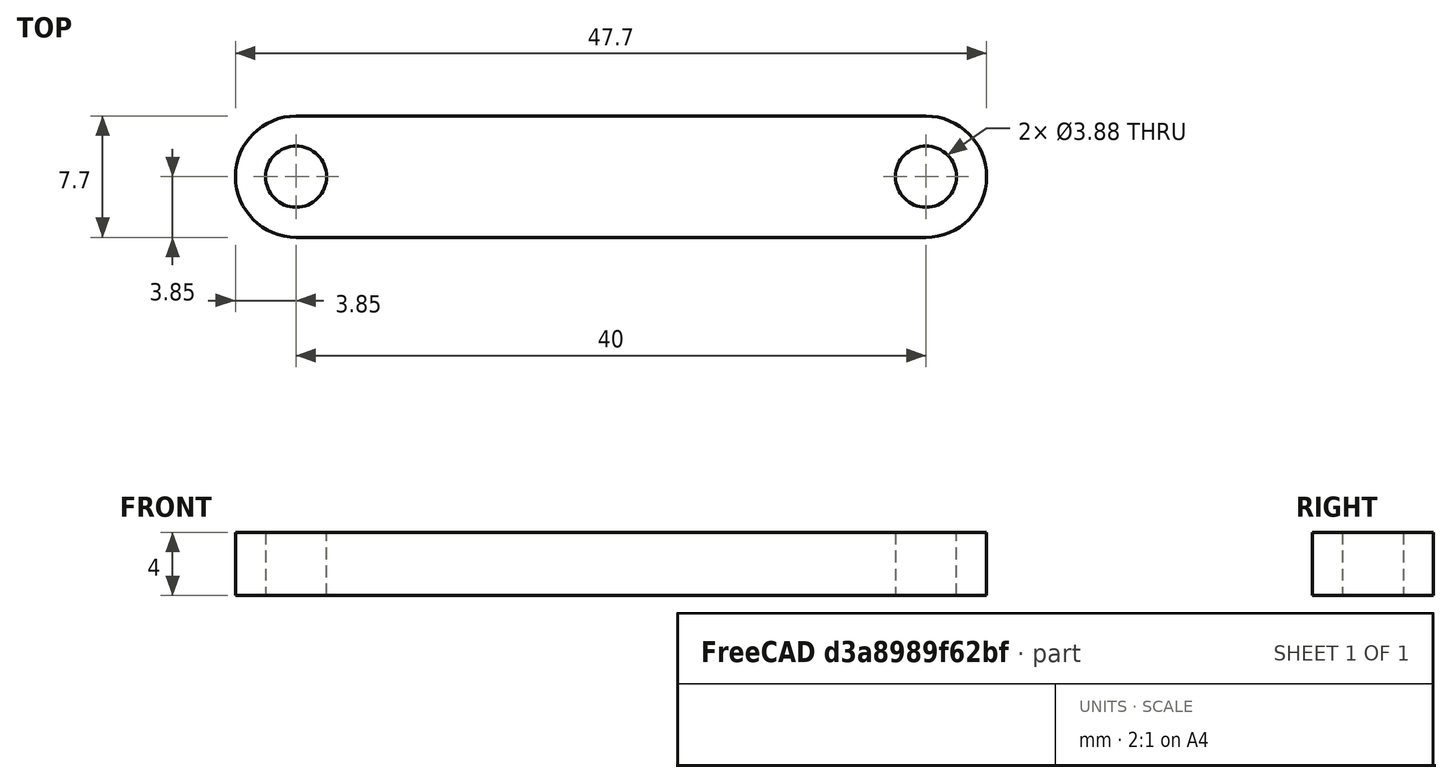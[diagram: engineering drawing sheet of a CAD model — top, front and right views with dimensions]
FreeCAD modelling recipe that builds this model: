
FCSTD DOCUMENT  (FreeCAD 0.20R29410 (Git))
Label: Eslabon1
License: All rights reserved
LicenseURL: http://en.wikipedia.org/wiki/All_rights_reserved
objects: Sketcher::SketchObject×1, Part::Extrusion×1
note: 2 computed .brp shape members not serialized (recipe doc carries the construction recipe); baked Part::Feature solids carry a one-line shape summary decoded from their .brp

FEATURE [Sketcher::SketchObject] Sketch  label="Eslabon 40x7.7mm, hoyo r1.94mm"
  FullyConstrained = true
  sketch-geometry (6):
    g0: LineSegment StartX=2e-16 StartY=3.85 StartZ=0 EndX=40 EndY=3.85 EndZ=0
    g1: LineSegment StartX=-7e-16 StartY=-3.85 StartZ=0 EndX=40 EndY=-3.85 EndZ=0
    g2: ArcOfCircle CenterX=0 CenterY=0 CenterZ=0 NormalX=0 NormalY=0 NormalZ=1 AngleXU=0 Radius=3.85 StartAngle=1.5708 EndAngle=4.71239
    g3: ArcOfCircle CenterX=40 CenterY=1e-16 CenterZ=0 NormalX=0 NormalY=0 NormalZ=1 AngleXU=0 Radius=3.85 StartAngle=4.71239 EndAngle=7.85398
    g4: Circle CenterX=0 CenterY=0 CenterZ=0 NormalX=0 NormalY=0 NormalZ=1 AngleXU=0 Radius=1.94
    g5: Circle CenterX=40 CenterY=1e-16 CenterZ=0 NormalX=0 NormalY=0 NormalZ=1 AngleXU=0 Radius=1.94
  constraints (17):
    c: PointOnObject(g0,g-2)
    c: PointOnObject(g1,g-2)
    c: Horizontal(g0)
    c: Horizontal(g1)
    c: Equal(g0,g1)
    c: Distance(g0) = 40
    c: DistanceY(g1,g0) = 7.7
    c: Coincident(g2,g-1)
    c: Coincident(g2,g0)
    c: Coincident(g3,g0)
    c: Coincident(g3,g1)
    c: Coincident(g4,g2)
    c: Coincident(g5,g3)
    c: Equal(g4,g5)
    c: Radius(g4) = 1.94
    c: Coincident(g1,g2)
    c: Radius(g3) = 3.85
FEATURE [Part::Extrusion] Extrude  label="Extrusion 4mm"
  Base = -> Sketch
  Dir = (0,0,1)
  DirMode = 2
  FaceMakerClass = Part::FaceMakerBullseye
  LengthFwd = 4
  LengthRev = 0
  Solid = true
  Symmetric = false
